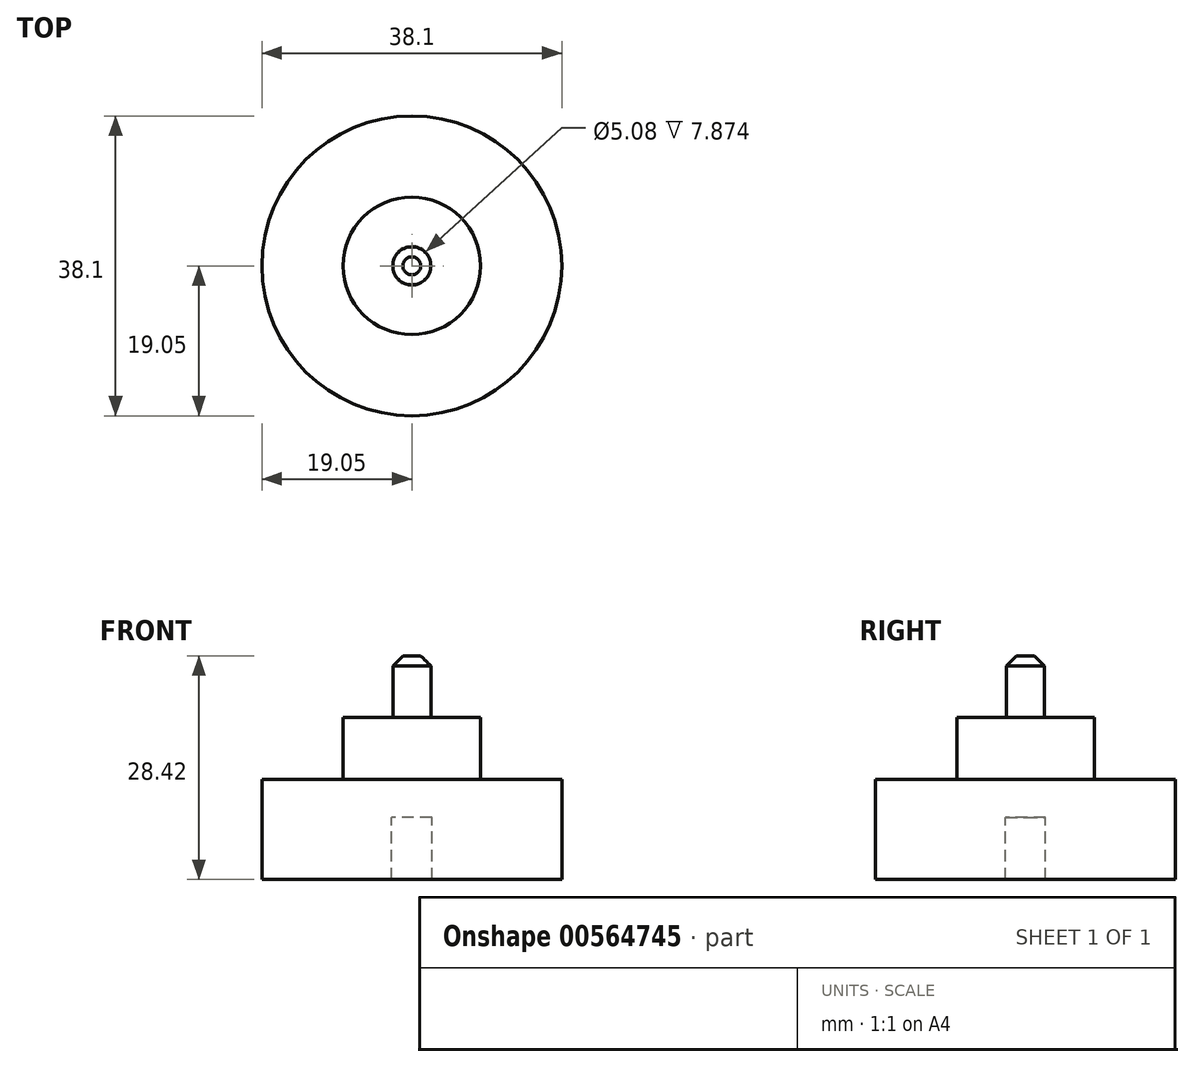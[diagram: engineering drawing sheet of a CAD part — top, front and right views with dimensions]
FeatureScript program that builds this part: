
annotation { "Feature Type Name" : "Feature", "Feature Type Description" : "" }
export const myFeature = defineFeature(function(context is Context, id is Id, definition is map)
    precondition{}
    {
        {
            var Q0;
            Q0=qCreatedBy(makeId("Front.planeOp"),FACE);
            var sketch = newSketch(context, id + "F0", { "sketchPlane" : qUnion([Q0])});
            skLineSegment(sketch, "E0", {"start": v(19.05, 0) * mm, "end": v(19.05, 12.7) * mm});
            skLineSegment(sketch, "E1", {"start": v(19.05, 12.7) * mm, "end": v(8.74, 12.7) * mm});
            skLineSegment(sketch, "E2", {"start": v(2.41, 20.57) * mm, "end": v(8.74, 20.57) * mm});
            skLineSegment(sketch, "E3", {"start": v(8.74, 20.57) * mm, "end": v(8.74, 12.7) * mm});
            skLineSegment(sketch, "E4", {"start": v(0, 28.42) * mm, "end": v(2.41, 28.42) * mm});
            skLineSegment(sketch, "E5", {"start": v(2.41, 28.42) * mm, "end": v(2.41, 20.57) * mm});
            skPoint(sketch, "E6.end.orphan", {"position": v(0, 20.57) * mm});
            skPoint(sketch, "E6.start.orphan", {"position": v(0, 12.7) * mm});
            skLineSegment(sketch, "E7", {"start": v(2.54, 0) * mm, "end": v(2.54, 7.87) * mm});
            skLineSegment(sketch, "E8", {"start": v(2.54, 7.87) * mm, "end": v(0, 7.87) * mm});
            skLineSegment(sketch, "E9", {"start": v(2.54, 0) * mm, "end": v(19.05, 0) * mm});
            skLineSegment(sketch, "E10", {"start": v(0, 28.42) * mm, "end": v(0, 7.87) * mm});
            skSolve(sketch);
        }
        {
            var Q0;
            Q0 = qSketchRegion(id + "F0", true);
            var Q1;
            Q1=sQuery(id+"F0.wireOp",EDGE,"E10");
            revolve(context, id + "F1", {"entities" : qUnion([Q0]), "axis" : qUnion([Q1]), "revolveType" : RevolveType.FULL});
        }
        {
            var Q0;
            Q0=makeQuery(id+"F1.opRevolve","SWEPT_EDGE",EDGE,{"disambiguationData":[OSD([sQuery(id+"F0.wireOp",EDGE,"E4"),sQuery(id+"F0.wireOp",EDGE,"E5")])]});
            chamfer(context, id + "F2", {"entities" : qUnion([Q0]), "width" : 1.27 * mm, "tangentPropagation" : true});
        }
    });
